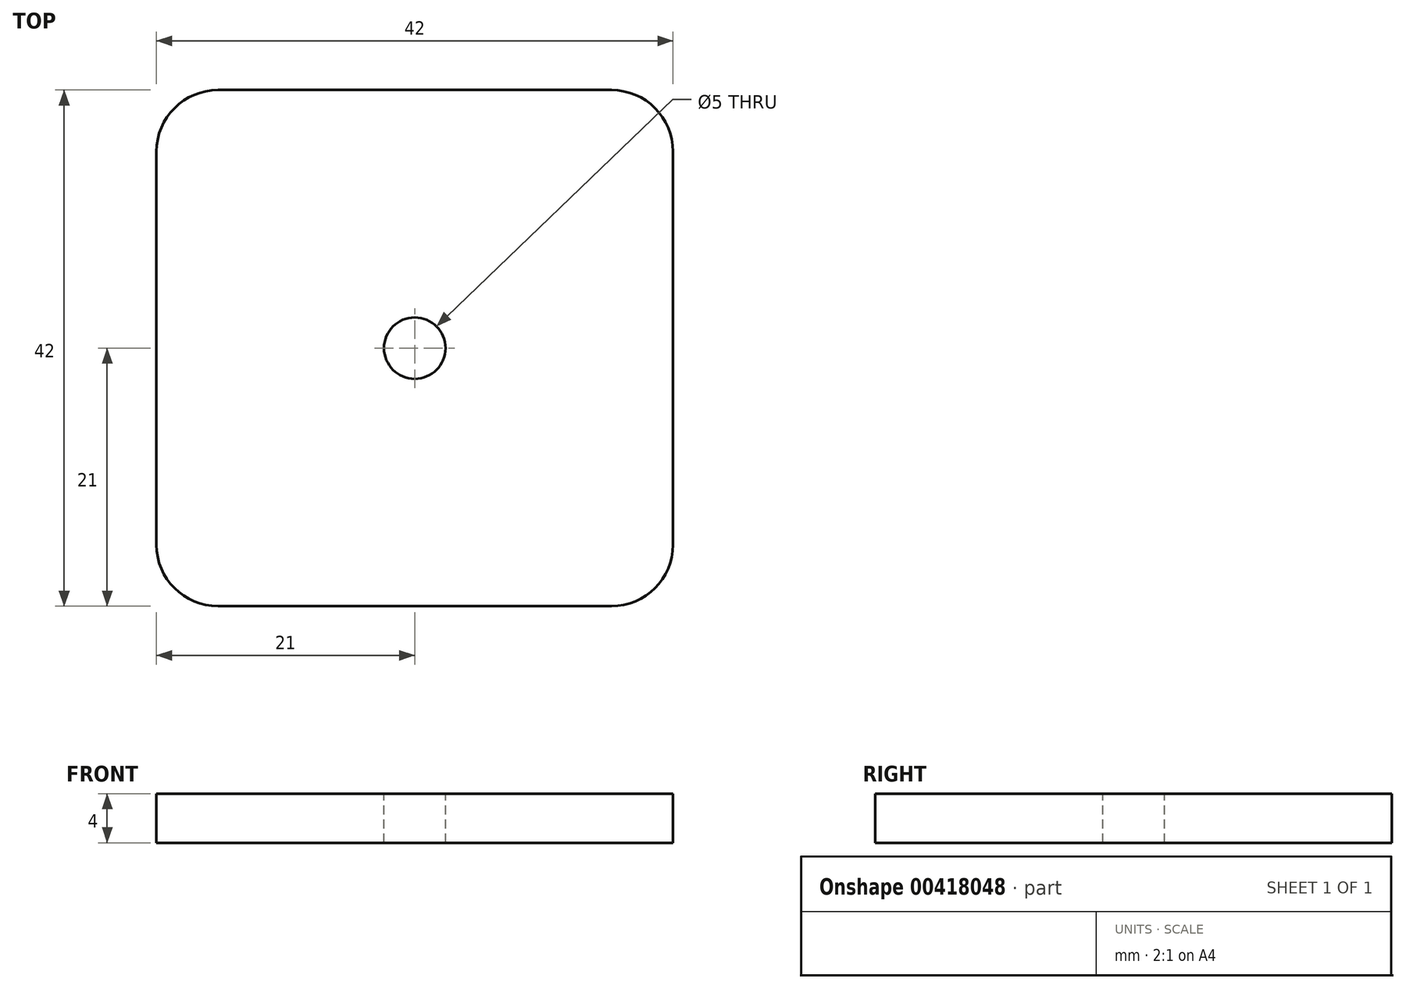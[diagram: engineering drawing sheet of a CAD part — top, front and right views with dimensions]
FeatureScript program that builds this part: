
annotation { "Feature Type Name" : "Feature", "Feature Type Description" : "" }
export const myFeature = defineFeature(function(context is Context, id is Id, definition is map)
    precondition{}
    {
        {
            var Q0;
            Q0=qCreatedBy(makeId("Top.planeOp"),FACE);
            var sketch = newSketch(context, id + "F0", { "sketchPlane" : qUnion([Q0])});
            skLineSegment(sketch, "E0.bottom", {"start": v(21, 21) * mm, "end": v(-21, 21) * mm});
            skLineSegment(sketch, "E0.top", {"start": v(21, -21) * mm, "end": v(-21, -21) * mm});
            skLineSegment(sketch, "E0.left", {"start": v(21, 21) * mm, "end": v(21, -21) * mm});
            skLineSegment(sketch, "E0.right", {"start": v(-21, 21) * mm, "end": v(-21, -21) * mm});
            skPoint(sketch, "E0.middle", {"position": v(0, 0) * mm});
            skSolve(sketch);
        }
        {
            var Q0;
            Q0=makeQuery(id+"F0.imprint","IMPRINT",FACE,{"disambiguationData":[TD([[makeQuery(id+"F0.imprint","IMPRINT",EDGE,{"derivedFrom":sQuery(id+"F0.wireOp",EDGE,"E0.bottom")}),1.0]])]});
            extrude(context, id + "F1", {"entities" : qUnion([Q0]), "depth" : 4 * mm});
        }
        {
            var Q0;
            Q0=makeQuery(id+"F1.opExtrude","CAP_FACE",FACE,{"disambiguationData":[OSD([sQuery(id+"F0.wireOp",EDGE,"E0.bottom"),sQuery(id+"F0.wireOp",EDGE,"E0.top"),sQuery(id+"F0.wireOp",EDGE,"E0.left"),sQuery(id+"F0.wireOp",EDGE,"E0.right")])],"isStart":false});
            var sketch = newSketch(context, id + "F2", { "sketchPlane" : qUnion([Q0])});
            skLineSegment(sketch, "E1.bottom", {"start": v(15.5, 15.5) * mm, "end": v(-15.5, 15.5) * mm});
            skLineSegment(sketch, "E1.top", {"start": v(15.5, -15.5) * mm, "end": v(-15.5, -15.5) * mm});
            skLineSegment(sketch, "E1.left", {"start": v(15.5, 15.5) * mm, "end": v(15.5, -15.5) * mm});
            skLineSegment(sketch, "E1.right", {"start": v(-15.5, 15.5) * mm, "end": v(-15.5, -15.5) * mm});
            skPoint(sketch, "E1.middle", {"position": v(0, 0) * mm});
            skSolve(sketch);
        }
        {
            var Q0;
            Q0=makeQuery(id+"F1.opExtrude","SWEPT_EDGE",EDGE,{"disambiguationData":[OSD([sQuery(id+"F0.wireOp",EDGE,"E0.bottom"),sQuery(id+"F0.wireOp",EDGE,"E0.right")])]});
            var Q1;
            Q1=makeQuery(id+"F1.opExtrude","SWEPT_EDGE",EDGE,{"disambiguationData":[OSD([sQuery(id+"F0.wireOp",EDGE,"E0.top"),sQuery(id+"F0.wireOp",EDGE,"E0.right")])]});
            var Q2;
            Q2=makeQuery(id+"F1.opExtrude","SWEPT_EDGE",EDGE,{"disambiguationData":[OSD([sQuery(id+"F0.wireOp",EDGE,"E0.top"),sQuery(id+"F0.wireOp",EDGE,"E0.left")])]});
            var Q3;
            Q3=makeQuery(id+"F1.opExtrude","SWEPT_EDGE",EDGE,{"disambiguationData":[OSD([sQuery(id+"F0.wireOp",EDGE,"E0.bottom"),sQuery(id+"F0.wireOp",EDGE,"E0.left")])]});
            fillet(context, id + "F3", {"entities" : qUnion([Q0, Q1, Q2, Q3]), "radius" : 5 * mm, "tangentPropagation" : true, "allowEdgeOverflow" : false});
        }
        {
            var Q0;
            Q0=makeQuery(id+"F2.imprint","IMPRINT",FACE,{"disambiguationData":[TD([[makeQuery(id+"F2.imprint","IMPRINT",EDGE,{"derivedFrom":sQuery(id+"F2.wireOp",EDGE,"E1.bottom")}),1.0]])]});
            var sketch = newSketch(context, id + "F4", { "sketchPlane" : qUnion([Q0])});
            skCircle(sketch, "E2", {"center": v(0, 0) * mm, "radius": 2.5 * mm});
            skSolve(sketch);
        }
        {
            var Q0;
            Q0 = qSketchRegion(id + "F4", true);
            extrude(context, id + "F5", {"entities" : qUnion([Q0]), "operationType" : NewBodyOperationType.REMOVE, "oppositeDirection" : true, "depth" : 25 * mm});
        }
    });
